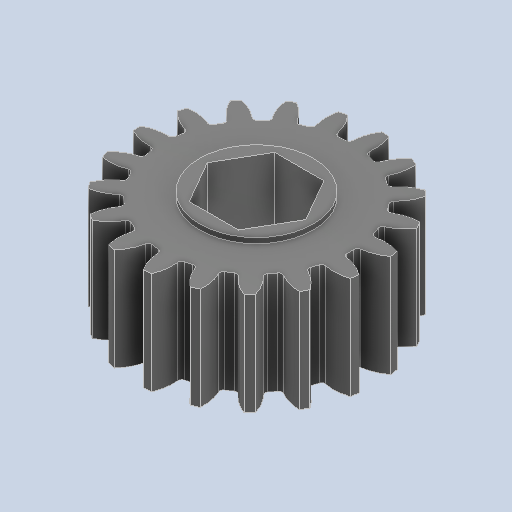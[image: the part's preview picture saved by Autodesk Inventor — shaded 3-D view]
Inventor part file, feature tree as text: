
AUTODESK INVENTOR PART (.ipt)
format: ipt  version: 2023.2 (Build 272271000, 271)  size: 250,880 bytes
history: native  units: in
note: dims shown in document units (in); Inventor stores cm internally (conversion verified against a paired STEP export)
features: fillet x1
ambient origin geometry x8: Origin, YZ Plane, XZ Plane, XY Plane, X Axis, Y Axis, Z Axis, Center Point
bodies: Solid1 (feature_tree)
feature tree (1):
  fillet  "Fillet1"  [1 undecoded]
note: 1 required parameter value undecoded (feature->parameter linkage not recoverable at this tier; creation-order binding heuristic only, values carry confidence <= 0.55)
